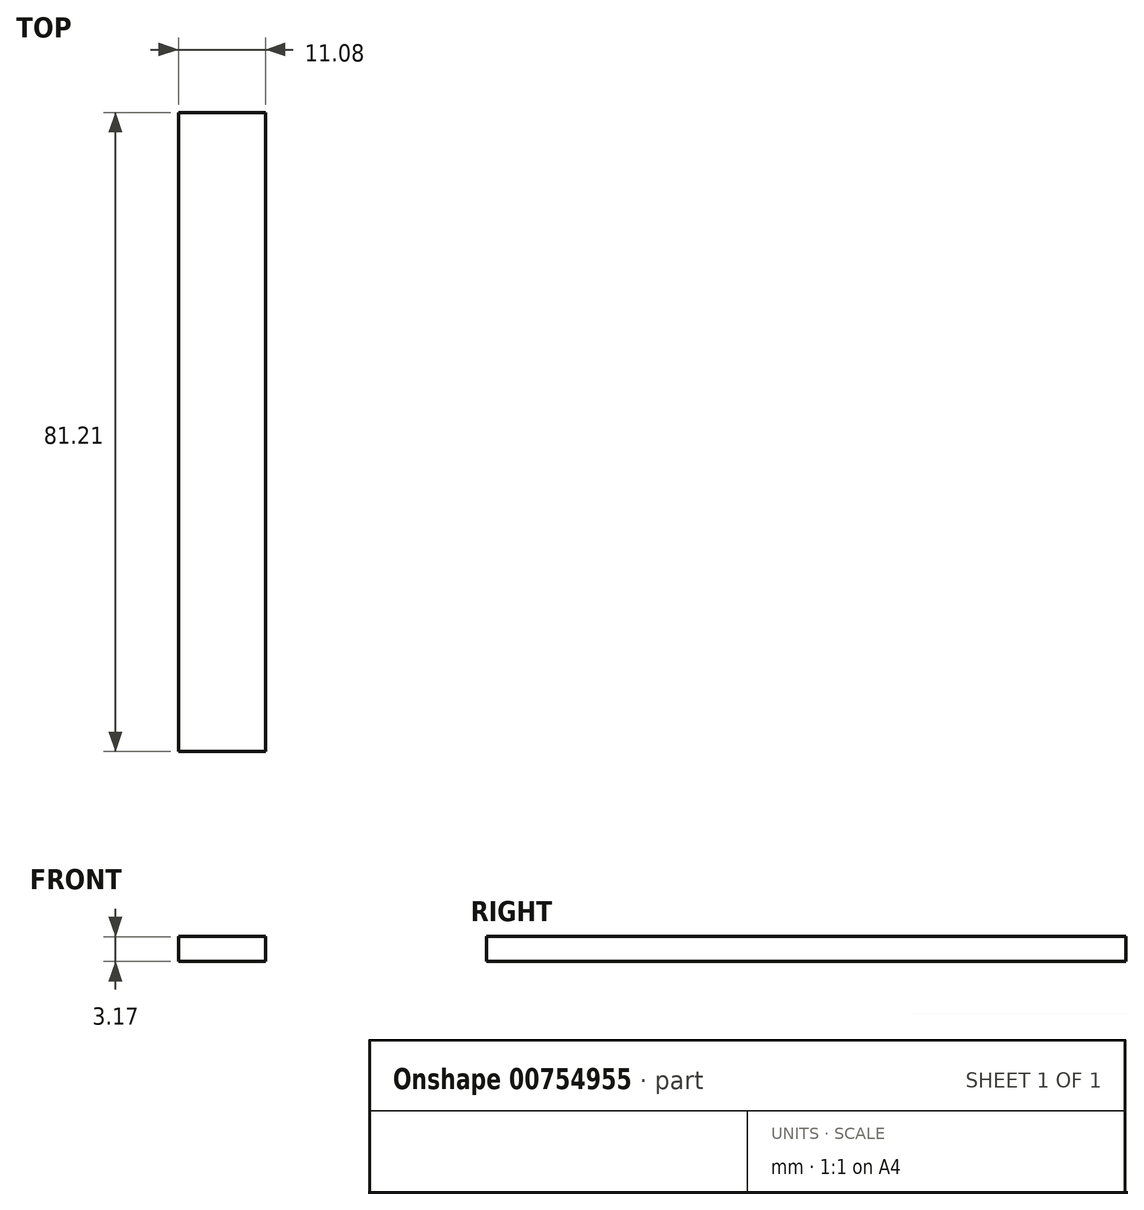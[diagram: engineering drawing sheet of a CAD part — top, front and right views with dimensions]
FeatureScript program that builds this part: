
annotation { "Feature Type Name" : "Feature", "Feature Type Description" : "" }
export const myFeature = defineFeature(function(context is Context, id is Id, definition is map)
    precondition{}
    {
        {
            var Q0;
            Q0=qCreatedBy(makeId("Top.planeOp"),FACE);
            var sketch = newSketch(context, id + "F0", { "sketchPlane" : qUnion([Q0])});
            skLineSegment(sketch, "E0.bottom", {"start": v(0, 26.8) * mm, "end": v(11.08, 26.8) * mm});
            skLineSegment(sketch, "E0.top", {"start": v(0, -54.41) * mm, "end": v(11.08, -54.41) * mm});
            skLineSegment(sketch, "E0.left", {"start": v(0, 26.8) * mm, "end": v(0, -54.41) * mm});
            skLineSegment(sketch, "E0.right", {"start": v(11.08, 26.8) * mm, "end": v(11.08, -54.41) * mm});
            skSolve(sketch);
        }
        {
            var Q0;
            Q0 = qSketchRegion(id + "F0", true);
            extrude(context, id + "F1", {"entities" : qUnion([Q0]), "depth" : 3.17 * mm, "offsetDistance" : 25.4 * mm});
        }
    });
